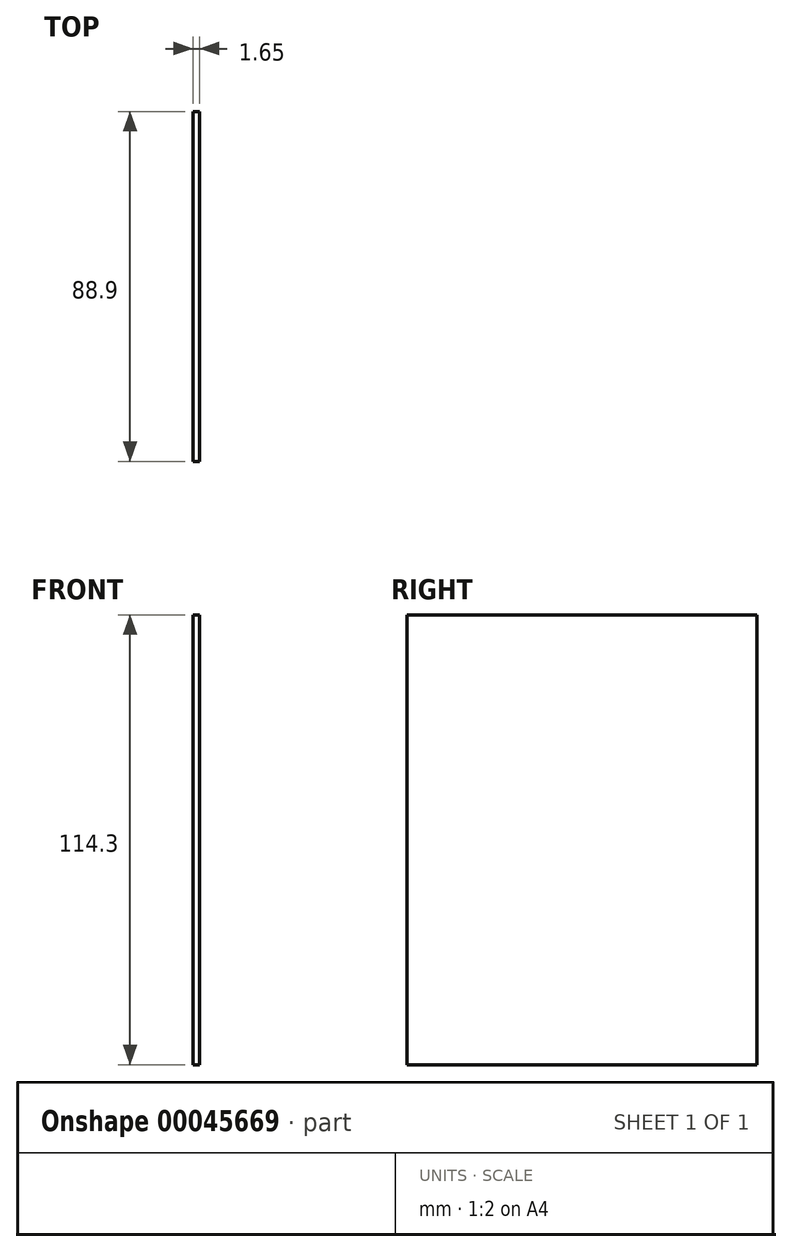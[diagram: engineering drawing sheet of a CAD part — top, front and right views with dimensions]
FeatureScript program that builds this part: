
annotation { "Feature Type Name" : "Feature", "Feature Type Description" : "" }
export const myFeature = defineFeature(function(context is Context, id is Id, definition is map)
    precondition{}
    {
        {
            var Q0;
            Q0=qCreatedBy(makeId("Right.planeOp"),FACE);
            var sketch = newSketch(context, id + "F0", { "sketchPlane" : qUnion([Q0])});
            skLineSegment(sketch, "E0.bottom", {"start": v(25.4, 60.53) * mm, "end": v(114.3, 60.53) * mm});
            skLineSegment(sketch, "E0.top", {"start": v(25.4, -53.77) * mm, "end": v(114.3, -53.77) * mm});
            skLineSegment(sketch, "E0.left", {"start": v(25.4, 60.53) * mm, "end": v(25.4, -53.77) * mm});
            skLineSegment(sketch, "E0.right", {"start": v(114.3, 60.53) * mm, "end": v(114.3, -53.77) * mm});
            skSolve(sketch);
        }
        {
            var Q0;
            Q0=makeQuery(id+"F0.imprint","IMPRINT",FACE,{"disambiguationData":[TD([[makeQuery(id+"F0.imprint","IMPRINT",EDGE,{"derivedFrom":sQuery(id+"F0.wireOp",EDGE,"E0.bottom")}),-1.0]])]});
            extrude(context, id + "F1", {"entities" : qUnion([Q0]), "depth" : 1.65 * mm});
        }
    });
